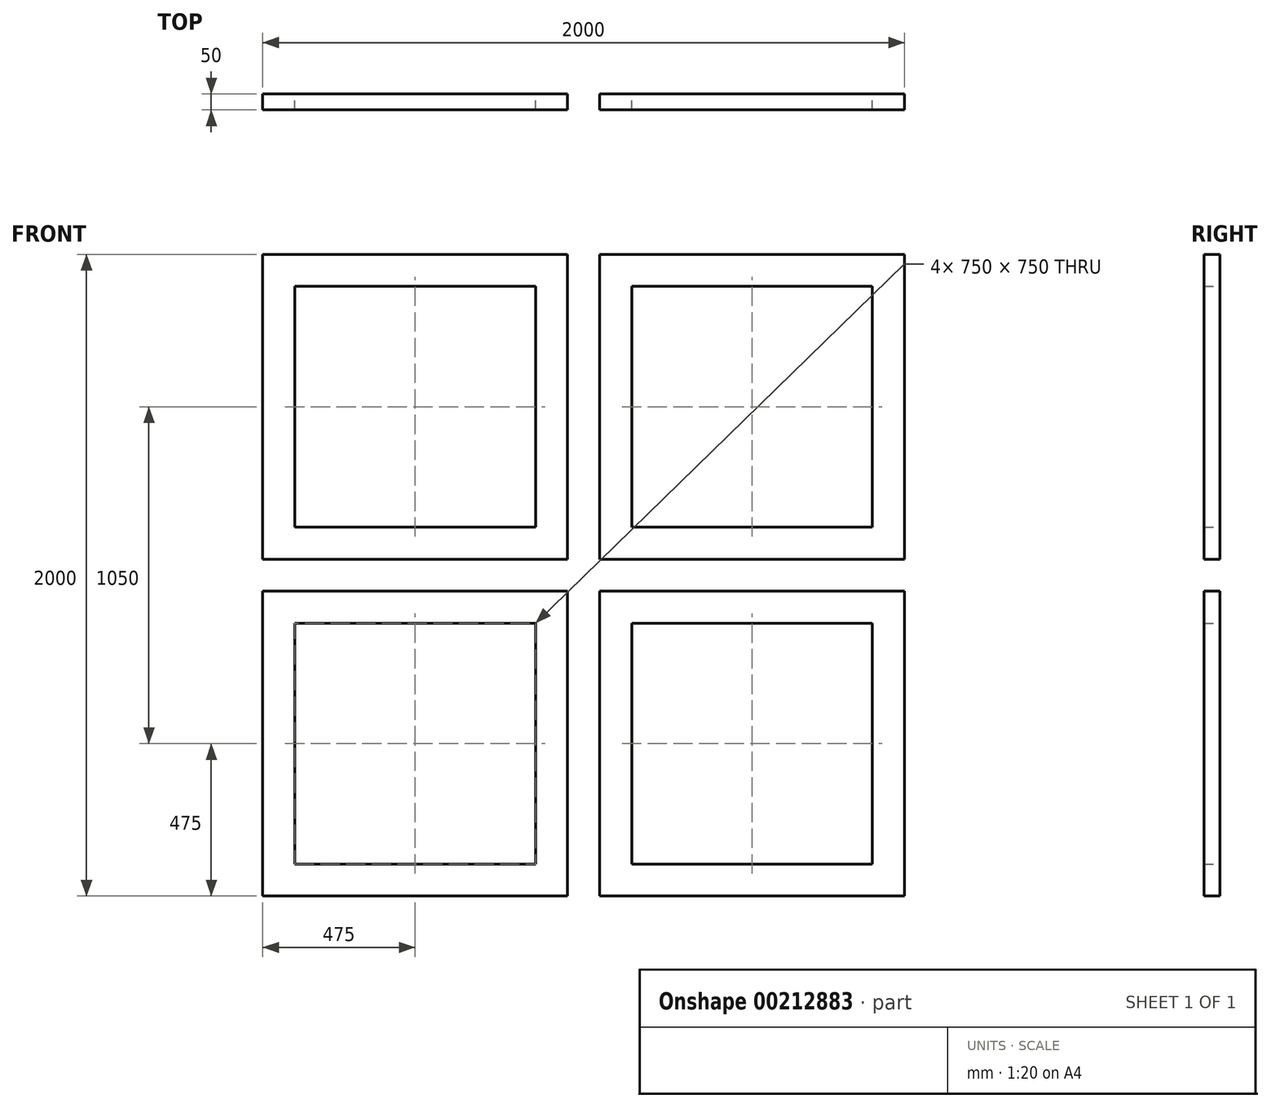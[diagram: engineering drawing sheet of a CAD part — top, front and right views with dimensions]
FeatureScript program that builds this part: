
annotation { "Feature Type Name" : "Feature", "Feature Type Description" : "" }
export const myFeature = defineFeature(function(context is Context, id is Id, definition is map)
    precondition{}
    {
        {
            var Q0;
            Q0=qCreatedBy(makeId("Front.planeOp"),FACE);
            var sketch = newSketch(context, id + "F0", { "sketchPlane" : qUnion([Q0])});
            skLineSegment(sketch, "E0.bottom", {"start": v(-900, 900) * mm, "end": v(-150, 900) * mm});
            skLineSegment(sketch, "E0.top", {"start": v(-900, -900) * mm, "end": v(-150, -900) * mm});
            skLineSegment(sketch, "E0.left", {"start": v(-900, 900) * mm, "end": v(-900, 150) * mm});
            skLineSegment(sketch, "E0.right", {"start": v(900, 900) * mm, "end": v(900, 150) * mm});
            skPoint(sketch, "E0.middle", {"position": v(0, 0) * mm});
            skLineSegment(sketch, "E1.bottom", {"start": v(-1000, 1000) * mm, "end": v(-50, 1000) * mm});
            skLineSegment(sketch, "E1.top", {"start": v(-1000, -1000) * mm, "end": v(-50, -1000) * mm});
            skLineSegment(sketch, "E1.left", {"start": v(-1000, 1000) * mm, "end": v(-1000, 50) * mm});
            skLineSegment(sketch, "E1.right", {"start": v(1000, 1000) * mm, "end": v(1000, 50) * mm});
            skLineSegment(sketch, "E2.left", {"start": v(-50, 1000) * mm, "end": v(-50, 50) * mm});
            skLineSegment(sketch, "E2.right", {"start": v(50, 1000) * mm, "end": v(50, 50) * mm});
            skLineSegment(sketch, "E3.bottom", {"start": v(-1000, -50) * mm, "end": v(-50, -50) * mm});
            skLineSegment(sketch, "E3.top", {"start": v(-1000, 50) * mm, "end": v(-50, 50) * mm});
            skLineSegment(sketch, "E4.left", {"start": v(-150, 900) * mm, "end": v(-150, 150) * mm});
            skLineSegment(sketch, "E4.right", {"start": v(150, 900) * mm, "end": v(150, 150) * mm});
            skLineSegment(sketch, "E5.bottom", {"start": v(-900, 150) * mm, "end": v(-150, 150) * mm});
            skLineSegment(sketch, "E5.top", {"start": v(-900, -150) * mm, "end": v(-150, -150) * mm});
            skPoint(sketch, "E6.orphan", {"position": v(-150, 1375.32) * mm});
            skPoint(sketch, "E7.orphan", {"position": v(150, 1375.32) * mm});
            skLineSegment(sketch, "E8.trimOffspring", {"start": v(50, 1000) * mm, "end": v(1000, 1000) * mm});
            skLineSegment(sketch, "E9.trimOffspring", {"start": v(150, 900) * mm, "end": v(900, 900) * mm});
            skLineSegment(sketch, "E10.trimOffspring", {"start": v(150, 150) * mm, "end": v(900, 150) * mm});
            skLineSegment(sketch, "E11.trimOffspring", {"start": v(50, 50) * mm, "end": v(1000, 50) * mm});
            skLineSegment(sketch, "E12.trimOffspring", {"start": v(50, -50) * mm, "end": v(1000, -50) * mm});
            skLineSegment(sketch, "E13.trimOffspring", {"start": v(150, -150) * mm, "end": v(900, -150) * mm});
            skLineSegment(sketch, "E14.trimOffspring", {"start": v(150, -900) * mm, "end": v(900, -900) * mm});
            skLineSegment(sketch, "E15.trimOffspring", {"start": v(-50, -50) * mm, "end": v(-50, -1000) * mm});
            skLineSegment(sketch, "E16.trimOffspring", {"start": v(-150, -150) * mm, "end": v(-150, -900) * mm});
            skLineSegment(sketch, "E17.trimOffspring", {"start": v(-900, -150) * mm, "end": v(-900, -900) * mm});
            skLineSegment(sketch, "E18.trimOffspring", {"start": v(-1000, -50) * mm, "end": v(-1000, -1000) * mm});
            skLineSegment(sketch, "E19.trimOffspring", {"start": v(50, -50) * mm, "end": v(50, -900) * mm});
            skLineSegment(sketch, "E20.trimOffspring", {"start": v(150, -150) * mm, "end": v(150, -900) * mm});
            skLineSegment(sketch, "E21.trimOffspring", {"start": v(900, -150) * mm, "end": v(900, -900) * mm});
            skLineSegment(sketch, "E22.trimOffspring", {"start": v(1000, -50) * mm, "end": v(1000, -1000) * mm});
            skLineSegment(sketch, "E23.bottom", {"start": v(150, -1000) * mm, "end": v(50, -1000) * mm});
            skLineSegment(sketch, "E23.right", {"start": v(50, -1000) * mm, "end": v(50, -900) * mm});
            skLineSegment(sketch, "E24.trimOffspring", {"start": v(50, -1000) * mm, "end": v(1000, -1000) * mm});
            skSolve(sketch);
        }
        {
            var Q0;
            Q0=qSketchRegion(id+"F0",true);
            extrude(context, id + "F1", {"entities" : qUnion([Q0]), "depth" : 50 * mm, "offsetDistance" : 25 * mm});
        }
    });
